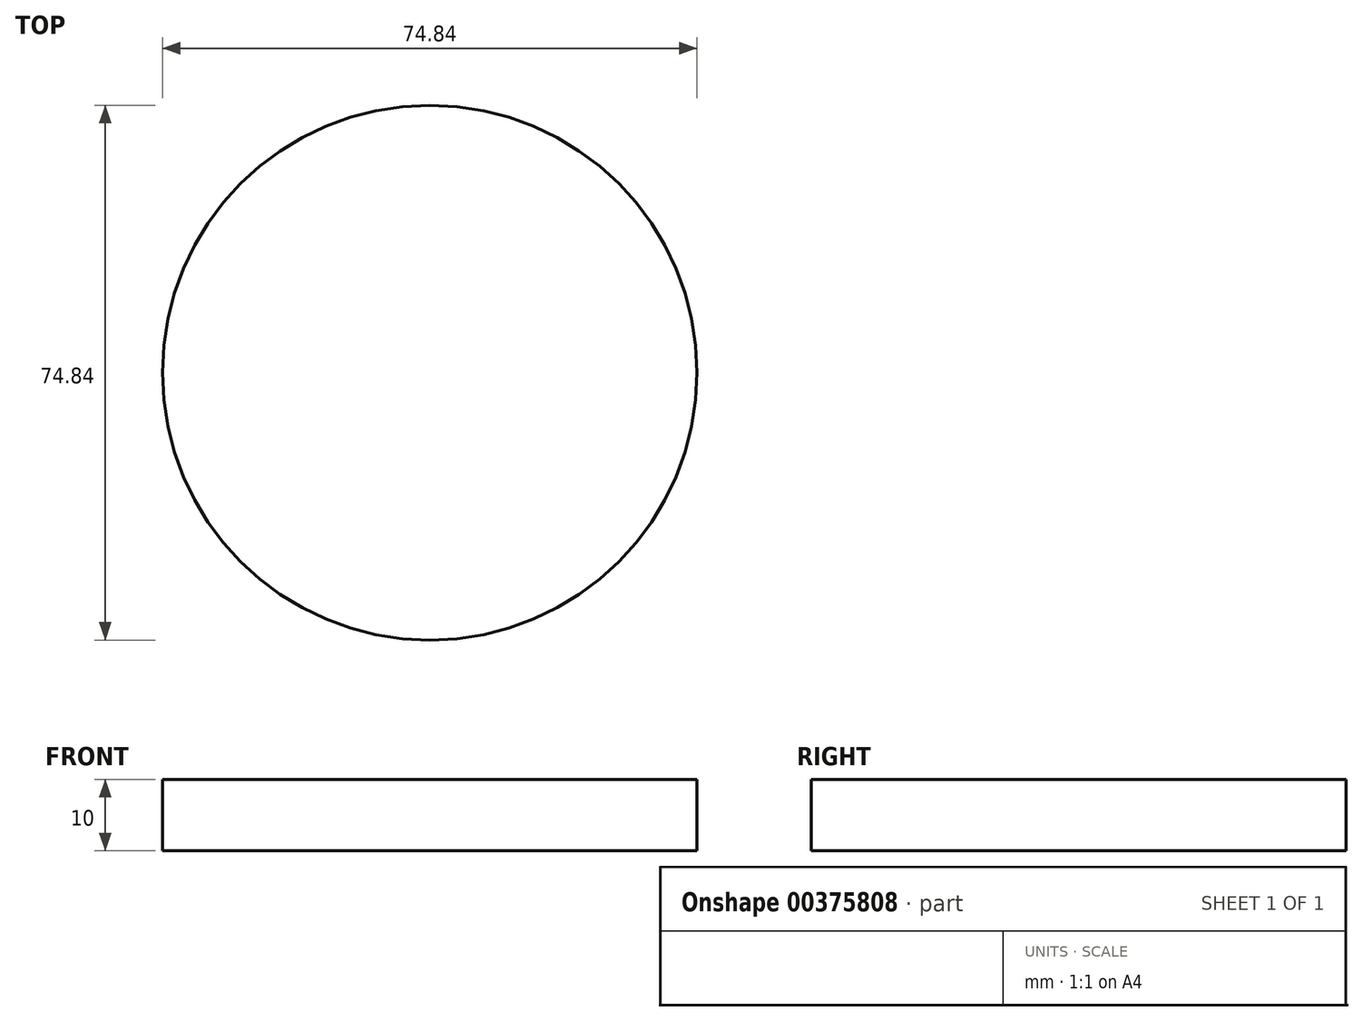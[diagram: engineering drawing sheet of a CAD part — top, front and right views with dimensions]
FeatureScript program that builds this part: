
annotation { "Feature Type Name" : "Feature", "Feature Type Description" : "" }
export const myFeature = defineFeature(function(context is Context, id is Id, definition is map)
    precondition{}
    {
        {
            var Q0;
            Q0=qCreatedBy(makeId("Top.planeOp"),FACE);
            var sketch = newSketch(context, id + "F0", { "sketchPlane" : qUnion([Q0])});
            skCircle(sketch, "E0", {"center": v(0, 0) * mm, "radius": 37.42 * mm});
            skArc(sketch, "E1", {"start": v(-2.24, 35.5) * mm, "mid": v(-5.4, 35.16) * mm, "end": v(-8.53, 34.54) * mm});
            skArc(sketch, "E2", {"start": v(-2.24, 35.5) * mm, "mid": v(-0.06, 33.46) * mm, "end": v(2.1, 35.51) * mm});
            skPoint(sketch, "E3.first.point", {"position": v(0, 33.46) * mm});
            skPoint(sketch, "E3.second.point", {"position": v(0, 35.57) * mm});
            skArc(sketch, "E4", {"start": v(35.5, 2.3) * mm, "mid": v(33.33, -0.06) * mm, "end": v(35.5, -2.44) * mm});
            skArc(sketch, "E5", {"start": v(2.32, -35.5) * mm, "mid": v(0.02, -33.38) * mm, "end": v(-2.28, -35.5) * mm});
            skArc(sketch, "E6", {"start": v(-35.5, -2.2) * mm, "mid": v(-33.46, 0.08) * mm, "end": v(-35.5, 2.37) * mm});
            skLineSegment(sketch, "E7", {"start": v(-34.44, 8.93) * mm, "end": v(-32.29, 5.44) * mm});
            skLineSegment(sketch, "E8", {"start": v(-32.29, 5.44) * mm, "end": v(-31.86, 6.4) * mm});
            skLineSegment(sketch, "E9", {"start": v(-31.86, 6.4) * mm, "end": v(-34.12, 10.08) * mm});
            skLineSegment(sketch, "E10", {"start": v(9, 34.42) * mm, "end": v(5.33, 32.31) * mm});
            skLineSegment(sketch, "E11", {"start": v(5.33, 32.31) * mm, "end": v(6.65, 32.31) * mm});
            skLineSegment(sketch, "E12", {"start": v(6.65, 32.31) * mm, "end": v(9.9, 34.17) * mm});
            skLineSegment(sketch, "E13.1.0", {"start": v(-34.3, -9.41) * mm, "end": v(-30.65, -11.54) * mm});
            skLineSegment(sketch, "E13.1.1", {"start": v(-31.3, -10.4) * mm, "end": v(-34.54, -8.52) * mm});
            skLineSegment(sketch, "E13.1.2", {"start": v(-30.65, -11.54) * mm, "end": v(-31.3, -10.4) * mm});
            skArc(sketch, "E13.1.3", {"start": v(-29.63, -19.7) * mm, "mid": v(-27.77, -22.23) * mm, "end": v(-25.7, -24.6) * mm});
            skLineSegment(sketch, "E13.2.0", {"start": v(25.3, -25) * mm, "end": v(25.32, -20.77) * mm});
            skLineSegment(sketch, "E13.2.1", {"start": v(24.66, -21.91) * mm, "end": v(24.65, -25.65) * mm});
            skLineSegment(sketch, "E13.2.2", {"start": v(25.32, -20.77) * mm, "end": v(24.66, -21.91) * mm});
            skArc(sketch, "E13.2.3", {"start": v(31.87, -15.81) * mm, "mid": v(33.15, -12.9) * mm, "end": v(34.17, -9.88) * mm});
            skArc(sketch, "E14.trimOffspring", {"start": v(9, 34.42) * mm, "mid": v(0.25, 35.57) * mm, "end": v(-8.53, 34.54) * mm});
            skArc(sketch, "E15.trimOffspring", {"start": v(9, 34.42) * mm, "mid": v(5.58, 35.13) * mm, "end": v(2.1, 35.51) * mm});
            skArc(sketch, "E16.trimOffspring", {"start": v(35.5, 2.3) * mm, "mid": v(35.16, 5.42) * mm, "end": v(34.54, 8.5) * mm});
            skLineSegment(sketch, "E17", {"start": v(34.43, -8.95) * mm, "end": v(32.3, -5.35) * mm});
            skLineSegment(sketch, "E18", {"start": v(32.3, -5.35) * mm, "end": v(32.1, -6.36) * mm});
            skLineSegment(sketch, "E19", {"start": v(32.1, -6.36) * mm, "end": v(34.17, -9.88) * mm});
            skArc(sketch, "E20.trimOffspring", {"start": v(34.43, -8.95) * mm, "mid": v(35.11, -5.72) * mm, "end": v(35.5, -2.44) * mm});
            skLineSegment(sketch, "E21", {"start": v(34.32, 9.34) * mm, "end": v(30.62, 11.43) * mm});
            skLineSegment(sketch, "E22", {"start": v(30.62, 11.43) * mm, "end": v(30.97, 10.51) * mm});
            skLineSegment(sketch, "E23", {"start": v(30.97, 10.51) * mm, "end": v(34.54, 8.5) * mm});
            skArc(sketch, "E24.trimOffspring", {"start": v(34.32, 9.34) * mm, "mid": v(30.97, 17.5) * mm, "end": v(25.71, 24.58) * mm});
            skLineSegment(sketch, "E25", {"start": v(25.06, 25.25) * mm, "end": v(20.87, 25.25) * mm});
            skLineSegment(sketch, "E26", {"start": v(20.87, 25.25) * mm, "end": v(21.67, 24.58) * mm});
            skLineSegment(sketch, "E27", {"start": v(21.67, 24.58) * mm, "end": v(25.71, 24.58) * mm});
            skArc(sketch, "E28.trimOffspring", {"start": v(25.06, 25.25) * mm, "mid": v(18.03, 30.66) * mm, "end": v(9.9, 34.17) * mm});
            skLineSegment(sketch, "E29", {"start": v(-9.38, 34.32) * mm, "end": v(-11.4, 30.62) * mm});
            skLineSegment(sketch, "E30", {"start": v(-11.4, 30.62) * mm, "end": v(-10.47, 30.98) * mm});
            skLineSegment(sketch, "E31", {"start": v(-10.47, 30.98) * mm, "end": v(-8.53, 34.54) * mm});
            skArc(sketch, "E32.trimOffspring", {"start": v(-9.38, 34.32) * mm, "mid": v(-17.5, 30.97) * mm, "end": v(-24.57, 25.73) * mm});
            skLineSegment(sketch, "E33", {"start": v(-25.25, 25.06) * mm, "end": v(-25.25, 20.69) * mm});
            skLineSegment(sketch, "E34", {"start": v(-25.25, 20.69) * mm, "end": v(-24.57, 21.7) * mm});
            skLineSegment(sketch, "E35", {"start": v(-24.57, 21.7) * mm, "end": v(-24.57, 25.73) * mm});
            skArc(sketch, "E36.trimOffspring", {"start": v(-25.25, 25.06) * mm, "mid": v(-30.61, 18.12) * mm, "end": v(-34.12, 10.08) * mm});
            skPoint(sketch, "E37.center.orphan", {"position": v(-34.44, 0) * mm});
            skArc(sketch, "E38.trimOffspring", {"start": v(-35.5, -2.2) * mm, "mid": v(-35.16, -5.38) * mm, "end": v(-34.54, -8.52) * mm});
            skLineSegment(sketch, "E39", {"start": v(-25.08, -25.23) * mm, "end": v(-20.82, -25.23) * mm});
            skLineSegment(sketch, "E40", {"start": v(-20.82, -25.23) * mm, "end": v(-21.76, -24.6) * mm});
            skLineSegment(sketch, "E41", {"start": v(-21.76, -24.6) * mm, "end": v(-25.7, -24.6) * mm});
            skArc(sketch, "E42.trimOffspring", {"start": v(-25.08, -25.23) * mm, "mid": v(-18.04, -30.66) * mm, "end": v(-9.89, -34.17) * mm});
            skLineSegment(sketch, "E43", {"start": v(-9.17, -34.37) * mm, "end": v(-5.4, -32.25) * mm});
            skLineSegment(sketch, "E44", {"start": v(-5.4, -32.25) * mm, "end": v(-6.6, -32.25) * mm});
            skLineSegment(sketch, "E45", {"start": v(-6.6, -32.25) * mm, "end": v(-9.89, -34.17) * mm});
            skArc(sketch, "E46.trimOffspring", {"start": v(-9.17, -34.37) * mm, "mid": v(-5.76, -35.1) * mm, "end": v(-2.28, -35.5) * mm});
            skArc(sketch, "E47.trimOffspring", {"start": v(2.32, -35.5) * mm, "mid": v(5.43, -35.16) * mm, "end": v(8.5, -34.54) * mm});
            skLineSegment(sketch, "E48", {"start": v(9.35, -34.32) * mm, "end": v(11.42, -30.59) * mm});
            skLineSegment(sketch, "E49", {"start": v(11.42, -30.59) * mm, "end": v(10.45, -31.1) * mm});
            skLineSegment(sketch, "E50", {"start": v(10.45, -31.1) * mm, "end": v(8.5, -34.54) * mm});
            skArc(sketch, "E51.trimOffspring", {"start": v(9.35, -34.32) * mm, "mid": v(17.54, -30.95) * mm, "end": v(24.65, -25.65) * mm});
            skArc(sketch, "E52.trimOffspring", {"start": v(-34.44, 8.93) * mm, "mid": v(-35.12, 5.67) * mm, "end": v(-35.5, 2.37) * mm});
            skArc(sketch, "E53.trimOffspring", {"start": v(-34.3, -9.41) * mm, "mid": v(-30.95, -17.54) * mm, "end": v(-25.7, -24.6) * mm});
            skArc(sketch, "E54.trimOffspring", {"start": v(-34.3, -9.41) * mm, "mid": v(-33.22, -12.73) * mm, "end": v(-31.8, -15.93) * mm});
            skArc(sketch, "E55.trimOffspring", {"start": v(25.3, -25) * mm, "mid": v(27.63, -22.4) * mm, "end": v(29.7, -19.58) * mm});
            skArc(sketch, "E56.trimOffspring", {"start": v(25.3, -25) * mm, "mid": v(30.68, -18) * mm, "end": v(34.17, -9.88) * mm});
            skSolve(sketch);
        }
        {
            var Q0;
            Q0=qSketchRegion(id+"F0",true);
            var Q1;
            {var subQ0=sQuery(id+"F0.wireOp",EDGE,"E2");var subQ1=sQuery(id+"F0.wireOp",EDGE,"E1");var subQ2=makeQuery(id+"F0.imprint","INTERSECT",VERTEX,{"disambiguationData":[OD(0.0)],"derivedFrom":[subQ1,subQ0]});Q1=makeQuery(id+"F0.imprint","IMPRINT",FACE,{"disambiguationData":[TD([[makeQuery(id+"F0.imprint","IMPRINT",EDGE,{"disambiguationData":[TD([[subQ2,1.0]])],"derivedFrom":subQ1}),1.0]])]});}
            var Q2;
            {var subQ0=sQuery(id+"F0.wireOp",EDGE,"E2");var subQ1=sQuery(id+"F0.wireOp",EDGE,"E1");var subQ2=makeQuery(id+"F0.imprint","INTERSECT",VERTEX,{"disambiguationData":[OD(1.0)],"derivedFrom":[subQ1,subQ0]});Q2=makeQuery(id+"F0.imprint","IMPRINT",FACE,{"disambiguationData":[TD([[makeQuery(id+"F0.imprint","IMPRINT",EDGE,{"disambiguationData":[TD([[subQ2,-1.0]])],"derivedFrom":subQ1}),1.0]])]});}
            var Q3;
            Q3=makeQuery(id+"F0.imprint","IMPRINT",FACE,{"disambiguationData":[TD([[makeQuery(id+"F0.imprint","IMPRINT",EDGE,{"derivedFrom":sQuery(id+"F0.wireOp",EDGE,"E10")}),1.0]])]});
            var Q4;
            {var subQ0=sQuery(id+"F0.wireOp",EDGE,"E2");Q4=makeQuery(id+"F0.imprint","IMPRINT",FACE,{"disambiguationData":[TD([[makeQuery(id+"F0.imprint","IMPRINT",EDGE,{"derivedFrom":subQ0}),1.0]])]});}
            extrude(context, id + "F1", {"entities" : qUnion([Q0, Q1, Q2, Q3, Q4]), "depth" : 10 * mm});
        }
    });
